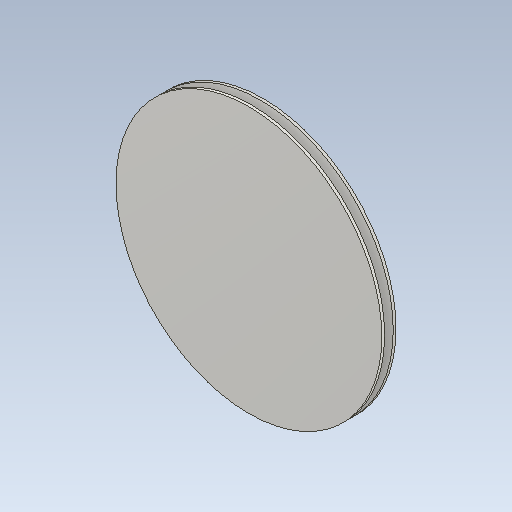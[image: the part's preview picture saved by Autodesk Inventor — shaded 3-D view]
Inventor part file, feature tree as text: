
AUTODESK INVENTOR PART (.ipt)
format: ipt  version: 2020.5 (Build 245400000, 400)  size: 113,664 bytes
history: native  units: mm (DEFAULTED — no unit token found)
features: other x3, fillet x2, sketch x1, pattern_linear x1
ambient origin geometry x8: Origin, YZ Plane, XZ Plane, XY Plane, X Axis, Y Axis, Z Axis, Center Point
bodies: Solid1 (feature_tree)
feature tree (7):
  sketch  "Boceto principal"  dims[d2=2.0mm d5=8.0mm d6=16.0mm d7=90.0deg d8=0.0mm d9=0.0mm d10=0.0mm d11=0.0mm d15=90.0deg d16=10.0mm d18=12.0mm d21=295.0mm d24=0.0mm d25=11.0mm d26=0.0mm d27=8.0mm]
  other  "Plano de correa"
  other  "Cuerpo"
  other  "Para ranuras"
  fillet  "Empalme externo"  Radius=8.5mm
  fillet  "Empalme interno"  Radius=5.934119mm
  pattern_linear  "Patrón para ranuras"  Spacing1=8.0mm  [1 undecoded]
note: 1 required parameter value undecoded (feature->parameter linkage not recoverable at this tier; creation-order binding heuristic only, values carry confidence <= 0.55)
